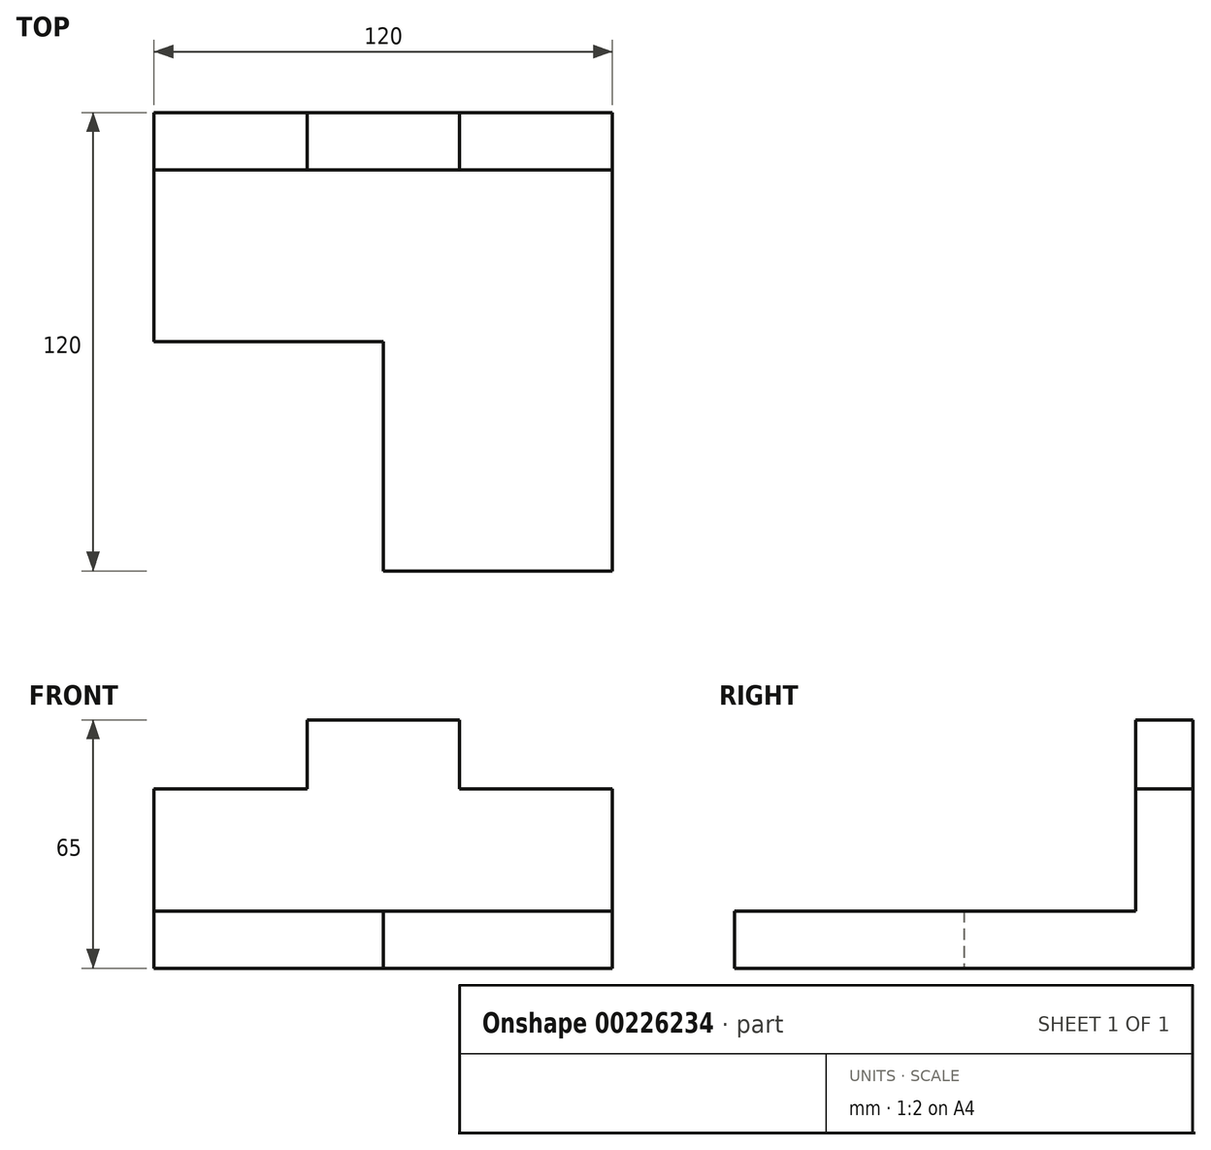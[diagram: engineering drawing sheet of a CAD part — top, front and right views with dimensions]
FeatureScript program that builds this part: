
annotation { "Feature Type Name" : "Feature", "Feature Type Description" : "" }
export const myFeature = defineFeature(function(context is Context, id is Id, definition is map)
    precondition{}
    {
        {
            var Q0;
            Q0=qCreatedBy(makeId("Top.planeOp"),FACE);
            var sketch = newSketch(context, id + "F0", { "sketchPlane" : qUnion([Q0])});
            skLineSegment(sketch, "E0.bottom", {"start": v(0, 0) * mm, "end": v(-120, 0) * mm});
            skLineSegment(sketch, "E0.top", {"start": v(0, -120) * mm, "end": v(-120, -120) * mm});
            skLineSegment(sketch, "E0.left", {"start": v(0, 0) * mm, "end": v(0, -120) * mm});
            skLineSegment(sketch, "E0.right", {"start": v(-120, 0) * mm, "end": v(-120, -120) * mm});
            skLineSegment(sketch, "E1.bottom", {"start": v(-120, -120) * mm, "end": v(-60, -120) * mm});
            skLineSegment(sketch, "E1.top", {"start": v(-120, -60) * mm, "end": v(-60, -60) * mm});
            skLineSegment(sketch, "E1.left", {"start": v(-120, -120) * mm, "end": v(-120, -60) * mm});
            skLineSegment(sketch, "E1.right", {"start": v(-60, -120) * mm, "end": v(-60, -60) * mm});
            skSolve(sketch);
        }
        {
            var Q0;
            Q0=makeQuery(id+"F0.imprint","IMPRINT",FACE,{"disambiguationData":[TD([[makeQuery(id+"F0.imprint","IMPRINT",EDGE,{"derivedFrom":sQuery(id+"F0.wireOp",EDGE,"E0.bottom")}),1.0]])]});
            extrude(context, id + "F1", {"entities" : qUnion([Q0]), "depth" : 15 * mm});
        }
        {
            var Q0;
            Q0=makeQuery(id+"F1.opExtrude","SWEPT_FACE",FACE,{"disambiguationData":[OSD([sQuery(id+"F0.wireOp",EDGE,"E0.bottom")])]});
            var sketch = newSketch(context, id + "F2", { "sketchPlane" : qUnion([Q0])});
            skLineSegment(sketch, "E2.bottom", {"start": v(0, 0) * mm, "end": v(120, 0) * mm});
            skLineSegment(sketch, "E2.top", {"start": v(0, 65) * mm, "end": v(120, 65) * mm});
            skLineSegment(sketch, "E2.left", {"start": v(0, 0) * mm, "end": v(0, 65) * mm});
            skLineSegment(sketch, "E2.right", {"start": v(120, 0) * mm, "end": v(120, 65) * mm});
            skLineSegment(sketch, "E3.bottom", {"start": v(0, 65) * mm, "end": v(40, 65) * mm});
            skLineSegment(sketch, "E3.top", {"start": v(0, 47) * mm, "end": v(40, 47) * mm});
            skLineSegment(sketch, "E3.left", {"start": v(0, 65) * mm, "end": v(0, 47) * mm});
            skLineSegment(sketch, "E3.right", {"start": v(40, 65) * mm, "end": v(40, 47) * mm});
            skLineSegment(sketch, "E4", {"start": v(60, 65) * mm, "end": v(60, 0) * mm, "construction": true});
            skLineSegment(sketch, "E5.MirrorCS", {"start": v(120, 47) * mm, "end": v(80, 47) * mm});
            skLineSegment(sketch, "E6.MirrorCS", {"start": v(80, 65) * mm, "end": v(80, 47) * mm});
            skSolve(sketch);
        }
        {
            var Q0;
            {var subQ4=sQuery(id+"F2.wireOp",EDGE,"E3.top");Q0=makeQuery(id+"F2.imprint","IMPRINT",FACE,{"disambiguationData":[TD([[makeQuery(id+"F2.imprint","IMPRINT",EDGE,{"derivedFrom":subQ4}),-1.0]])]});}
            extrude(context, id + "F3", {"entities" : qUnion([Q0]), "operationType" : NewBodyOperationType.ADD, "oppositeDirection" : true, "depth" : 15 * mm});
        }
    });
